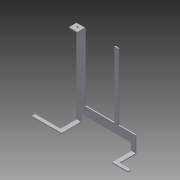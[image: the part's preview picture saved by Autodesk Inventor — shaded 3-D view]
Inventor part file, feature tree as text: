
AUTODESK INVENTOR PART (.ipt)
format: ipt  version: 2013 (Build 170138000, 138)  size: 266,240 bytes
history: native  units: in
note: dims shown in document units (in); Inventor stores cm internally (conversion verified against a paired STEP export)
features: sheet_metal_op x11, other x7, sketch x6, projected_geometry x1
ambient origin geometry x8: Origin, YZ Plane, XZ Plane, XY Plane, X Axis, Y Axis, Z Axis, Center Point
bodies: Solid1 (feature_tree)
feature tree (25):
  sheet_metal_op  "Face1"
  sheet_metal_op  "Flange1"
  sheet_metal_op  "Flange2"
  sheet_metal_op  "Face2"
  sheet_metal_op  "Face4"
  sketch  "Sketch1"  dims[d0=8.0in]
  other  "Plate1"
  sketch  "Sketch2"  dims[d1=1.0in]
  other  "Plate2"
  sheet_metal_op  "Bend1"
  sheet_metal_op  "Corner1"
  sketch  "Sketch3"  dims[d2=5.95in]
  other  "Plate3"
  sheet_metal_op  "Bend2"
  sheet_metal_op  "Corner2"
  sketch  "Sketch4"  dims[d3=1.0in]
  sketch  "Sketch5"  dims[d4=1.0in]
  projected_geometry  "Projected Loop1"
  other  "Plate4"
  sheet_metal_op  "Bend3"
  sketch  "Sketch7"  dims[d5=0.5in d6=1.0in d7=0.5in d8=0.0in d9=1.0in d10=1.0in d11=0.125in d12=0.125in d13=0.0625in d14=0.25in d15=0.125in d16=2.375in d17=90.0deg d18=0.05in d19=0.5in d20=0.125in d21=0.125in d22=0.125in d23=0.0625in d24=0.25in d25=0.125in d26=1.0in d27=90.0deg d28=0.05in d29=0.5in d30=0.125in d31=0.125in d32=0.19in d33=0.5in d34=0.5in d35=0.125in d36=0.0in d37=3.0in d38=0.375in d39=1.375in d40=0.375in d41=0.125in d42=0.125in d43=0.0625in d44=0.25in d45=0.125in d55=0.125in d56=0.125in d57=0.0625in d58=0.25in d59=0.125in d60=0.5in d61=2.0in d62=7.825in]
  other  "Plate6"
  sheet_metal_op  "Bend5"
  other  "Cut1"
  other  "Definition1"
